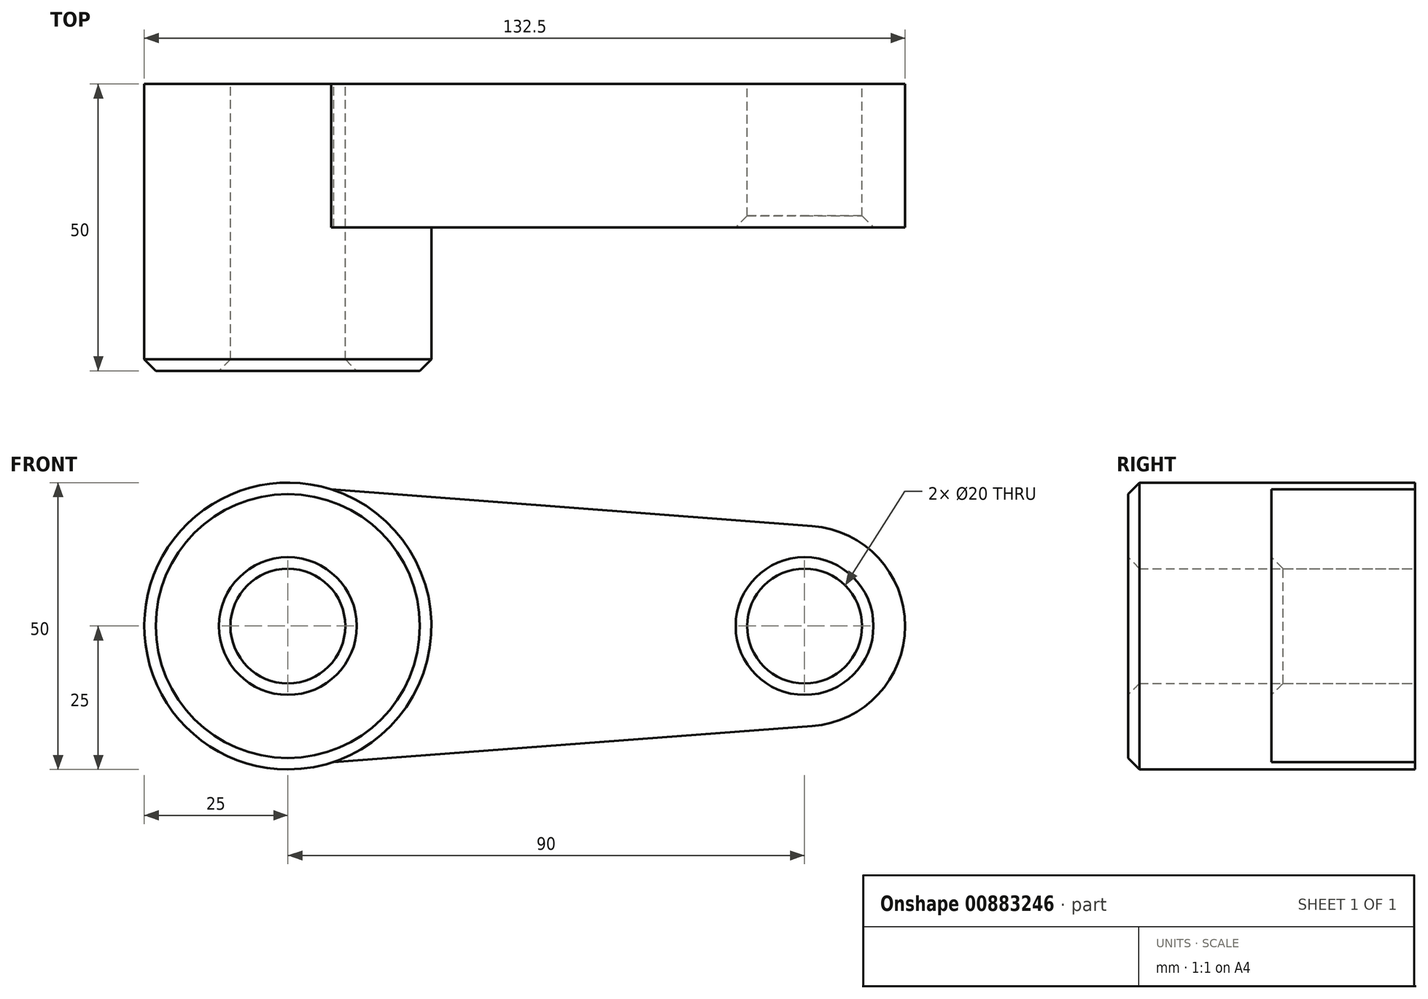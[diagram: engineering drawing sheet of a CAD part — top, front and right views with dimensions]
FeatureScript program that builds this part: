
annotation { "Feature Type Name" : "Feature", "Feature Type Description" : "" }
export const myFeature = defineFeature(function(context is Context, id is Id, definition is map)
    precondition{}
    {
        {
            var Q0;
            Q0=qCreatedBy(makeId("Front.planeOp"),FACE);
            var sketch = newSketch(context, id + "F0", { "sketchPlane" : qUnion([Q0])});
            skCircle(sketch, "E0", {"center": v(0, 0) * mm, "radius": 25 * mm});
            skCircle(sketch, "E1", {"center": v(90, 0) * mm, "radius": 17.5 * mm});
            skLineSegment(sketch, "E2", {"start": v(7.51, 23.84) * mm, "end": v(91.33, 17.45) * mm});
            skLineSegment(sketch, "E3", {"start": v(7.99, -23.69) * mm, "end": v(91.3, -17.45) * mm});
            skCircle(sketch, "E4", {"center": v(0, 0) * mm, "radius": 10 * mm});
            skCircle(sketch, "E5", {"center": v(90, 0) * mm, "radius": 10 * mm});
            skSolve(sketch);
        }
        {
            var Q0;
            Q0=makeQuery(id+"F0.imprint","IMPRINT",FACE,{"disambiguationData":[TD([[makeQuery(id+"F0.imprint","IMPRINT",EDGE,{"derivedFrom":sQuery(id+"F0.wireOp",EDGE,"E4")}),-1.0]])]});
            var Q1;
            Q1 = qSketchRegion(id + "F0", true);
            var Q2;
            Q2=makeQuery(id+"F0.imprint","IMPRINT",FACE,{"disambiguationData":[TD([[makeQuery(id+"F0.imprint","IMPRINT",EDGE,{"derivedFrom":sQuery(id+"F0.wireOp",EDGE,"E5")}),-1.0]])]});
            var Q3;
            {var subQ0=sQuery(id+"F0.wireOp",EDGE,"E2");Q3=makeQuery(id+"F0.imprint","IMPRINT",FACE,{"disambiguationData":[TD([[makeQuery(id+"F0.imprint","IMPRINT",EDGE,{"derivedFrom":subQ0}),-1.0]])]});}
            extrude(context, id + "F1", {"entities" : qUnion([Q0, Q1, Q2, Q3]), "depth" : 25 * mm, "offsetDistance" : 25 * mm});
        }
        {
            var Q0;
            Q0=makeQuery(id+"F0.imprint","IMPRINT",FACE,{"disambiguationData":[TD([[makeQuery(id+"F0.imprint","IMPRINT",EDGE,{"derivedFrom":sQuery(id+"F0.wireOp",EDGE,"E4")}),-1.0]])]});
            extrude(context, id + "F2", {"entities" : qUnion([Q0]), "operationType" : NewBodyOperationType.ADD, "depth" : 50 * mm, "offsetDistance" : 25 * mm});
        }
        {
            var Q0;
            Q0=makeQuery(id+"F2.opExtrude","CAP_EDGE",EDGE,{"disambiguationData":[OSD([sQuery(id+"F0.wireOp",EDGE,"E0")])],"isStart":false});
            var Q1;
            Q1=makeQuery(id+"F2.opExtrude","CAP_EDGE",EDGE,{"disambiguationData":[OSD([sQuery(id+"F0.wireOp",EDGE,"E4")])],"isStart":false});
            var Q2;
            Q2=makeQuery(id+"F1.opExtrude","CAP_EDGE",EDGE,{"disambiguationData":[OSD([sQuery(id+"F0.wireOp",EDGE,"E5")])],"isStart":false});
            chamfer(context, id + "F3", {"entities" : qUnion([Q0, Q1, Q2]), "width" : 2 * mm, "tangentPropagation" : true});
        }
    });
